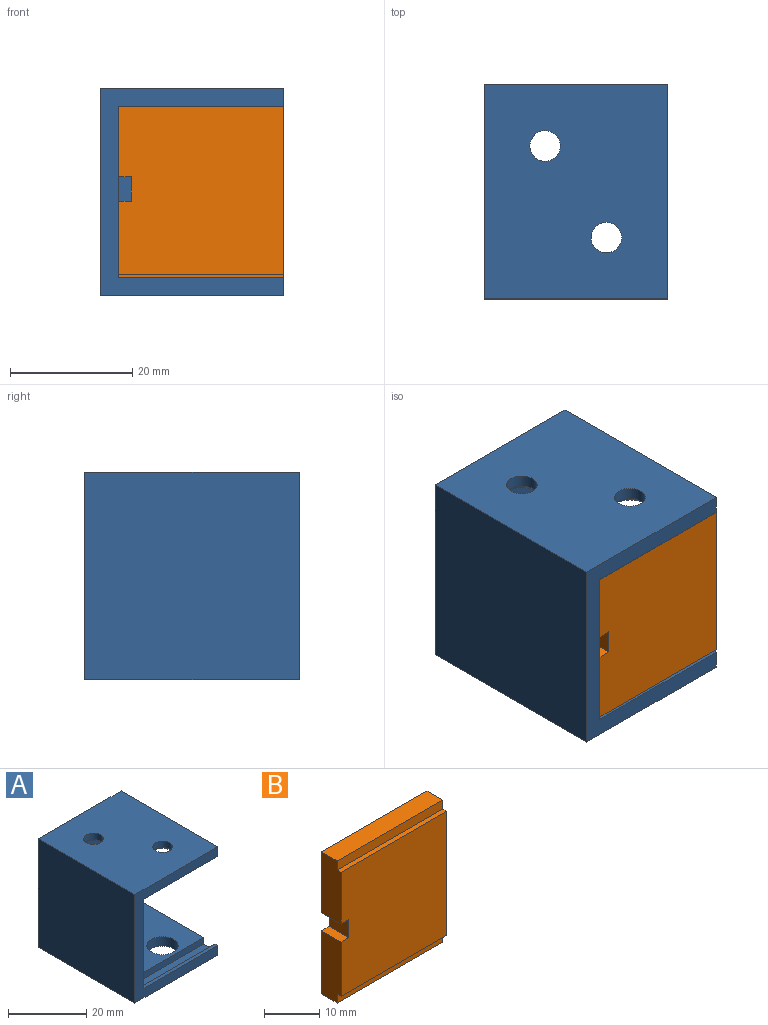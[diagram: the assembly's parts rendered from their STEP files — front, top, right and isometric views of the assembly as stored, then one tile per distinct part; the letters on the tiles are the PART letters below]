
ASSEMBLY  parts=2 mates=1
PART A: 24 faces, bbox 30x35x34 mm
  f0: plane 34x30mm, normal (0,-1,0), area 264mm2, adj f2,f3,f4,f5,f7,f8,f17
  f1: plane 34x30mm, normal (0,1,0), area 1020mm2, adj f2,f3,f4,f5
  f2: plane 35x34mm, normal (-1,0,0), area 1190mm2, adj f0,f1,f4,f5
  f3: plane 35x34mm, normal (1,0,0), area 278mm2, adj f0,f1,f4,f5,f6,f7,f8,f9
  f4: plane 35x30mm, normal (0,0,-1), area 949.5mm2, adj f0,f1,f2,f3,f20,f21
  f5: plane 35x30mm, normal (0,0,1), area 1010.7mm2, adj f0,f1,f2,f3,f18,f19
  f6: plane 27x2mm, normal (0,1,0), area 54mm2, adj f3,f7,f16,f17
  f7: plane 27x1mm, normal (0,0,-1), area 27mm2, adj f0,f3,f6,f17
  f8: plane 27x1mm, normal (0,0,1), area 27mm2, adj f0,f3,f9,f17
  f9: plane 27x2mm, normal (0,1,0), area 54mm2, adj f3,f8,f10,f17
  f10: plane 27x4mm, normal (0,0,1), area 108mm2, adj f3,f9,f11,f17
  f11: plane 27x2mm, normal (0,-1,0), area 54mm2, adj f3,f10,f12,f17
  f12: plane 27x27mm, normal (0,0,1), area 628.5mm2, adj f3,f11,f13,f17,f20,f21
  f13: plane 28x27mm, normal (0,-1,0), area 756mm2, adj f3,f12,f14,f17
  f14: plane 27x27mm, normal (0,0,-1), area 652mm2, adj f3,f13,f15,f17,f22,f23
  f15: plane 27x2mm, normal (0,-1,0), area 54mm2, adj f3,f14,f16,f17
  f16: plane 27x4mm, normal (0,0,-1), area 108mm2, adj f3,f6,f15,f17
  f17: plane 32x32mm, normal (1,0,0), area 912mm2, adj f0,f6,f7,f8,f9,f10,f11,f12
  f18: cylinder r=2.5mm len=5mm, axis (0,0,1), area 31.4mm2, adj f5,f22
  f19: cylinder r=2.5mm len=5mm, axis (0,0,1), area 31.4mm2, adj f5,f23
  f20: cylinder r=4mm len=8mm, axis (0,0,-1), area 75.4mm2, adj f4,f12
  f21: cylinder r=4mm len=8mm, axis (0,0,-1), area 75.4mm2, adj f4,f12
  f22: cone r=3.5mm half-angle=45deg, axis (0,0,-1), area 26.7mm2, adj f14,f18
  f23: cone r=3.5mm half-angle=45deg, axis (0,0,-1), area 26.7mm2, adj f14,f19
PART B: 14 faces, bbox 27x5x31.5 mm
  f0: plane 14x5mm, normal (-1,0,0), area 68mm2, adj f1,f2,f4,f5,f6,f12
  f1: plane 27.5x27mm, normal (0,-1,0), area 734.5mm2, adj f0,f3,f4,f9,f10,f11,f12,f13
  f2: plane 31.5x27mm, normal (0,1,0), area 842.5mm2, adj f0,f6,f7,f9,f10,f11,f12,f13
  f3: plane 27x1mm, normal (0,0,1), area 27mm2, adj f1,f8,f9,f10
  f4: plane 27x1mm, normal (0,0,-1), area 27mm2, adj f0,f1,f5,f9
  f5: plane 27x2mm, normal (0,-1,0), area 54mm2, adj f0,f4,f6,f9
  f6: plane 27x4mm, normal (0,0,-1), area 108mm2, adj f0,f2,f5,f9
  f7: plane 27x4mm, normal (0,0,1), area 108mm2, adj f2,f8,f9,f10
  f8: plane 27x2mm, normal (0,-1,0), area 54mm2, adj f3,f7,f9,f10
  f9: plane 31.5x5mm, normal (1,0,0), area 153.5mm2, adj f1,f2,f3,f4,f5,f6,f7,f8
  f10: plane 13.5x5mm, normal (-1,0,0), area 65.5mm2, adj f1,f2,f3,f7,f8,f11
  f11: plane 5x2mm, normal (0,0,-1), area 10mm2, adj f1,f2,f10,f13
  f12: plane 5x2mm, normal (0,0,1), area 10mm2, adj f0,f1,f2,f13
  f13: plane 5x4mm, normal (-1,0,0), area 20mm2, adj f1,f2,f11,f12
PLACE A t=(1.01,10.79,-3.66)mm
PLACE B t=(-17.92,38.16,-40)mm
MATE slider B.f10 <-> A.f17  axis (-1,0,0) through (-17.92,-14.79,-4.66)mm
